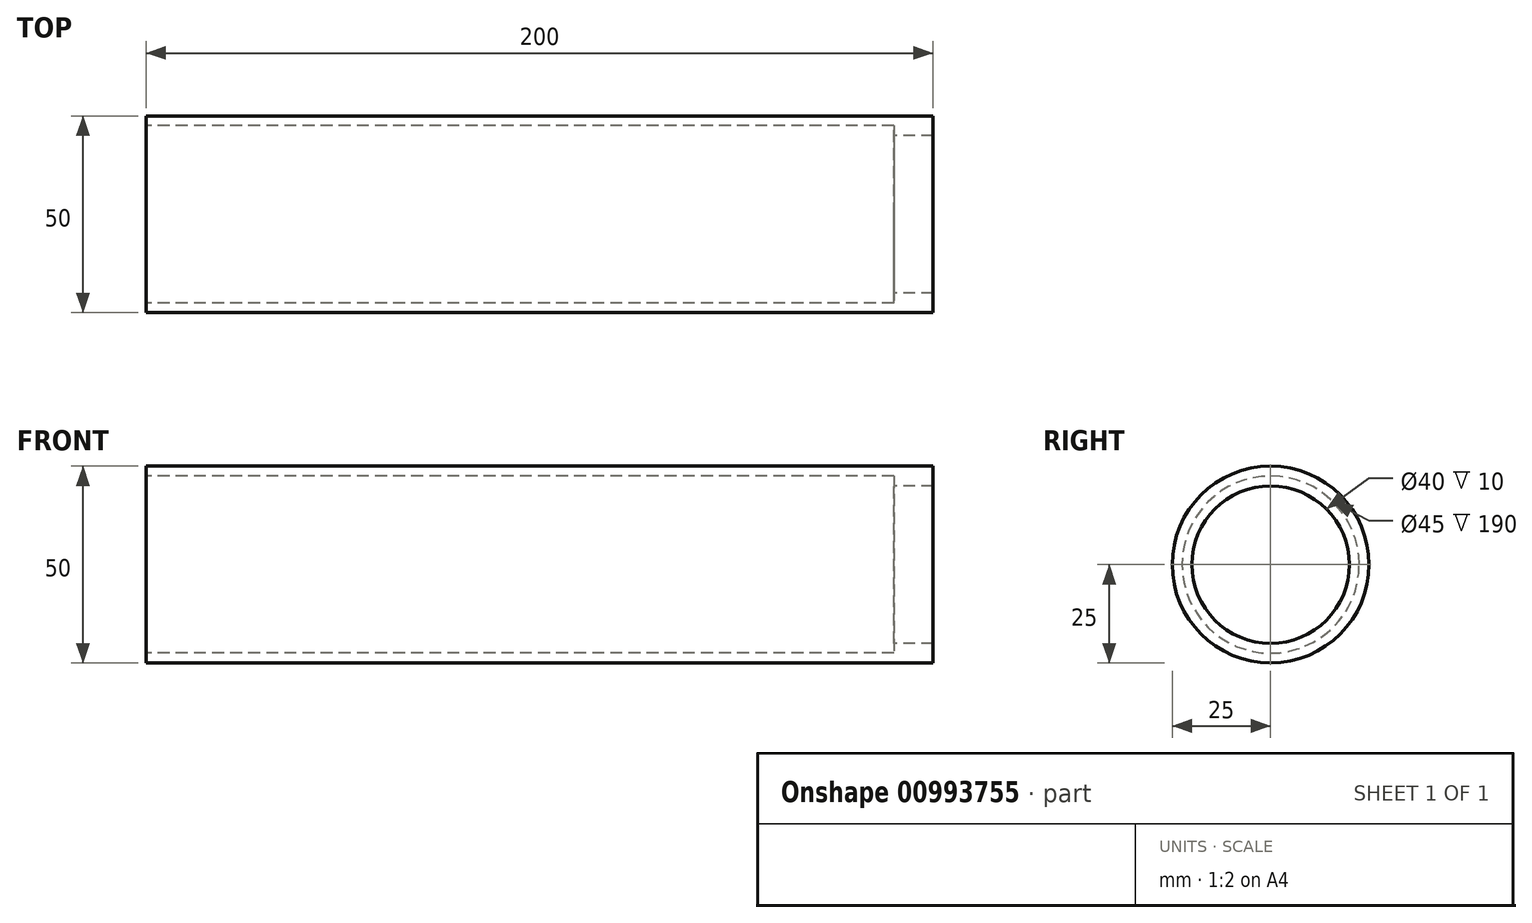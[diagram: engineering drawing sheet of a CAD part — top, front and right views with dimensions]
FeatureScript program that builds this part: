
annotation { "Feature Type Name" : "Feature", "Feature Type Description" : "" }
export const myFeature = defineFeature(function(context is Context, id is Id, definition is map)
    precondition{}
    {
        {
            var Q0;
            Q0=qCreatedBy(makeId("Right.planeOp"),FACE);
            var sketch = newSketch(context, id + "F0", { "sketchPlane" : qUnion([Q0])});
            skCircle(sketch, "E0", {"center": v(0, 0) * mm, "radius": 25 * mm});
            skCircle(sketch, "E1", {"center": v(0, 0) * mm, "radius": 20 * mm});
            skSolve(sketch);
        }
        {
            var Q0;
            Q0 = qSketchRegion(id + "F0", true);
            extrude(context, id + "F1", {"entities" : qUnion([Q0]), "endBound" : BoundingType.SYMMETRIC, "depth" : 200 * mm, "offsetDistance" : 25 * mm});
        }
        {
            var Q0;
            Q0=makeQuery(id+"F1.opExtrude","CAP_FACE",FACE,{"disambiguationData":[OSD([sQuery(id+"F0.wireOp",EDGE,"E0"),sQuery(id+"F0.wireOp",EDGE,"E1")])],"isStart":true});
            var sketch = newSketch(context, id + "F2", { "sketchPlane" : qUnion([Q0])});
            skCircle(sketch, "E2", {"center": v(0, 0) * mm, "radius": 22.5 * mm});
            skSolve(sketch);
        }
        {
            var Q0;
            Q0=makeQuery(id+"F2.imprint","IMPRINT",FACE,{"disambiguationData":[TD([[makeQuery(id+"F2.imprint","IMPRINT",EDGE,{"derivedFrom":sQuery(id+"F2.wireOp",EDGE,"E2")}),1.0]])]});
            extrude(context, id + "F3", {"entities" : qUnion([Q0]), "operationType" : NewBodyOperationType.REMOVE, "oppositeDirection" : true, "depth" : 190 * mm, "offsetDistance" : 25 * mm});
        }
    });
